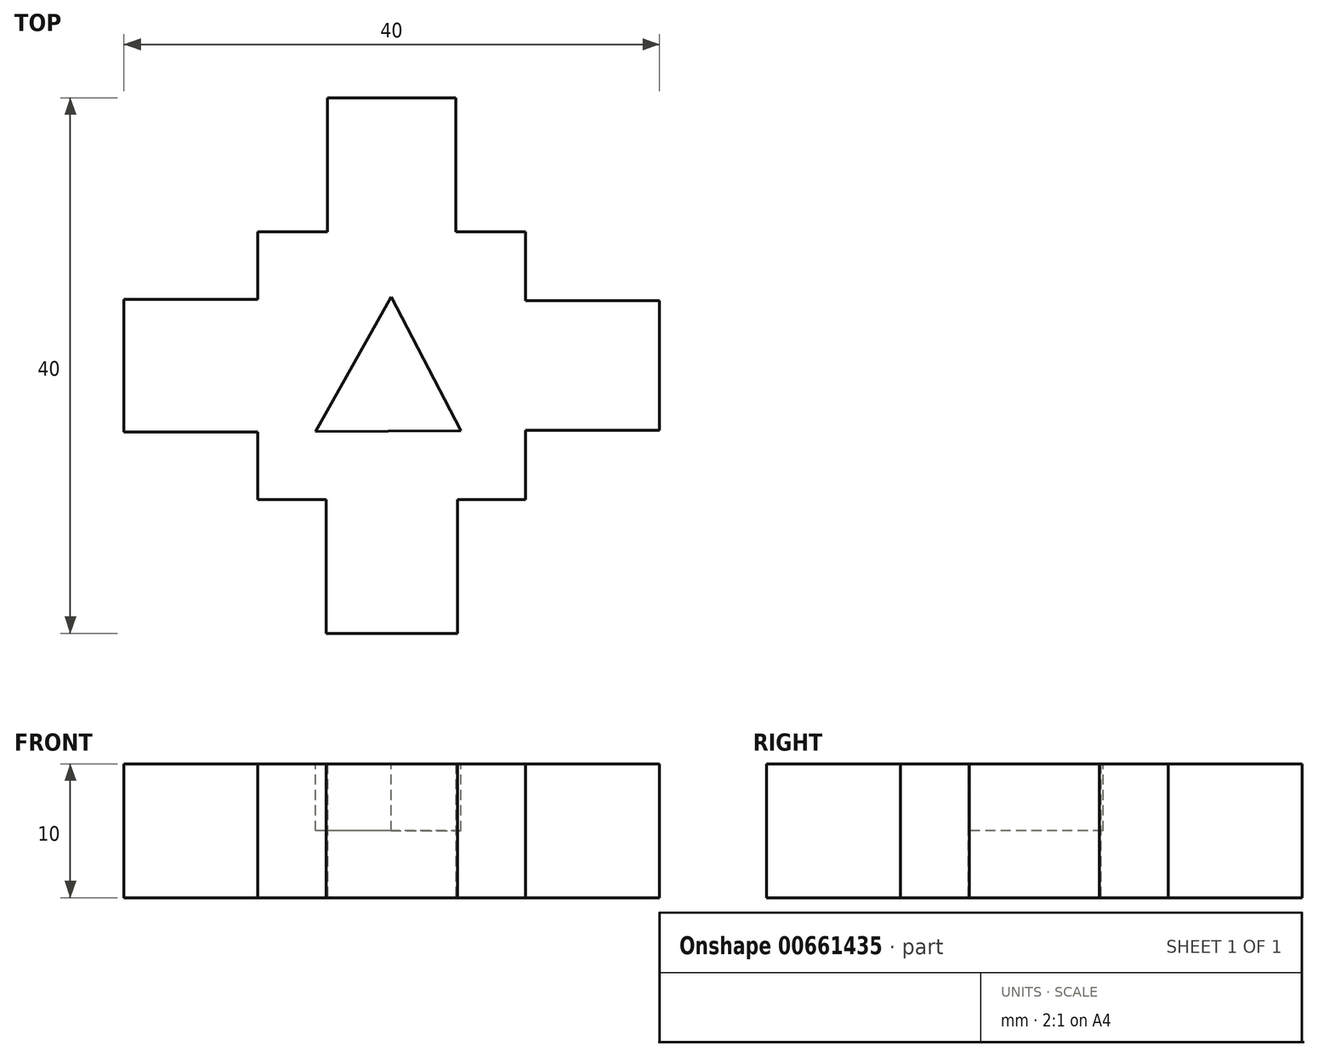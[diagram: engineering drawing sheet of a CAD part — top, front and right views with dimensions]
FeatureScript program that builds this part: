
annotation { "Feature Type Name" : "Feature", "Feature Type Description" : "" }
export const myFeature = defineFeature(function(context is Context, id is Id, definition is map)
    precondition{}
    {
        {
            var Q0;
            Q0=qCreatedBy(makeId("Top.planeOp"),FACE);
            var sketch = newSketch(context, id + "F0", { "sketchPlane" : qUnion([Q0])});
            skLineSegment(sketch, "E0", {"start": v(0, 0) * mm, "end": v(20, 0) * mm});
            skLineSegment(sketch, "E1", {"start": v(20, 0) * mm, "end": v(20, -20) * mm});
            skLineSegment(sketch, "E2", {"start": v(20, -20) * mm, "end": v(0, -20) * mm});
            skLineSegment(sketch, "E3", {"start": v(0, -20) * mm, "end": v(0, 0) * mm});
            skLineSegment(sketch, "E4", {"start": v(0, -10) * mm, "end": v(-10, -10) * mm});
            skLineSegment(sketch, "E5", {"start": v(10, 0) * mm, "end": v(10, 10) * mm});
            skLineSegment(sketch, "E6", {"start": v(20, -10) * mm, "end": v(30, -10) * mm});
            skLineSegment(sketch, "E7", {"start": v(10, -20) * mm, "end": v(10, -30) * mm});
            skLineSegment(sketch, "E8", {"start": v(10, 10) * mm, "end": v(5.2, 10) * mm});
            skLineSegment(sketch, "E9", {"start": v(10, 10) * mm, "end": v(14.8, 10) * mm});
            skLineSegment(sketch, "E10", {"start": v(14.8, 10) * mm, "end": v(14.8, 0) * mm});
            skLineSegment(sketch, "E11", {"start": v(5.2, 10) * mm, "end": v(5.2, 0) * mm});
            skLineSegment(sketch, "E12", {"start": v(30, -10) * mm, "end": v(30, -5.15) * mm});
            skLineSegment(sketch, "E13", {"start": v(30, -10) * mm, "end": v(30, -14.85) * mm});
            skLineSegment(sketch, "E14", {"start": v(30, -14.85) * mm, "end": v(20, -14.85) * mm});
            skLineSegment(sketch, "E15", {"start": v(30, -5.15) * mm, "end": v(20, -5.15) * mm});
            skLineSegment(sketch, "E16", {"start": v(10, -30) * mm, "end": v(14.9, -30) * mm});
            skLineSegment(sketch, "E17", {"start": v(14.9, -30) * mm, "end": v(14.9, -20) * mm});
            skLineSegment(sketch, "E18", {"start": v(10, -30) * mm, "end": v(5.1, -30) * mm});
            skLineSegment(sketch, "E19", {"start": v(5.1, -30) * mm, "end": v(5.1, -20) * mm});
            skLineSegment(sketch, "E20", {"start": v(-10, -10) * mm, "end": v(-10, -5.05) * mm});
            skLineSegment(sketch, "E21", {"start": v(-10, -5.05) * mm, "end": v(0, -5.05) * mm});
            skLineSegment(sketch, "E22", {"start": v(-10, -10) * mm, "end": v(-10, -14.95) * mm});
            skLineSegment(sketch, "E23", {"start": v(-10, -14.95) * mm, "end": v(0, -14.95) * mm});
            skSolve(sketch);
        }
        {
            var Q0;
            Q0=qSketchRegion(id+"F0",true);
            extrude(context, id + "F1", {"entities" : qUnion([Q0]), "depth" : 10 * mm, "offsetDistance" : 25 * mm});
        }
        {
            var Q0;
            Q0=makeQuery(id+"F1.opExtrude","CAP_FACE",FACE,{"disambiguationData":[OSD([sQuery(id+"F0.wireOp",EDGE,"E0"),sQuery(id+"F0.wireOp",EDGE,"E1"),sQuery(id+"F0.wireOp",EDGE,"E2"),sQuery(id+"F0.wireOp",EDGE,"E3"),sQuery(id+"F0.wireOp",EDGE,"E8"),sQuery(id+"F0.wireOp",EDGE,"E9"),sQuery(id+"F0.wireOp",EDGE,"E10"),sQuery(id+"F0.wireOp",EDGE,"E11"),sQuery(id+"F0.wireOp",EDGE,"E12"),sQuery(id+"F0.wireOp",EDGE,"E13"),sQuery(id+"F0.wireOp",EDGE,"E14"),sQuery(id+"F0.wireOp",EDGE,"E15"),sQuery(id+"F0.wireOp",EDGE,"E16"),sQuery(id+"F0.wireOp",EDGE,"E17"),sQuery(id+"F0.wireOp",EDGE,"E18"),sQuery(id+"F0.wireOp",EDGE,"E19"),sQuery(id+"F0.wireOp",EDGE,"E20"),sQuery(id+"F0.wireOp",EDGE,"E21"),sQuery(id+"F0.wireOp",EDGE,"E22"),sQuery(id+"F0.wireOp",EDGE,"E23")])],"isStart":false});
            var sketch = newSketch(context, id + "F2", { "sketchPlane" : qUnion([Q0])});
            skLineSegment(sketch, "E24", {"start": v(20, -14.85) * mm, "end": v(0, -14.95) * mm});
            skLineSegment(sketch, "E25", {"start": v(10, -14.9) * mm, "end": v(9.95, -4.87) * mm});
            skLineSegment(sketch, "E26", {"start": v(9.95, -4.87) * mm, "end": v(4.3, -14.93) * mm});
            skLineSegment(sketch, "E27", {"start": v(9.95, -4.87) * mm, "end": v(15.18, -14.87) * mm});
            skSolve(sketch);
        }
        {
            var Q0;
            Q0=qSketchRegion(id+"F2",true);
            extrude(context, id + "F3", {"entities" : qUnion([Q0]), "operationType" : NewBodyOperationType.REMOVE, "oppositeDirection" : true, "depth" : 5 * mm, "offsetDistance" : 25 * mm});
        }
    });
